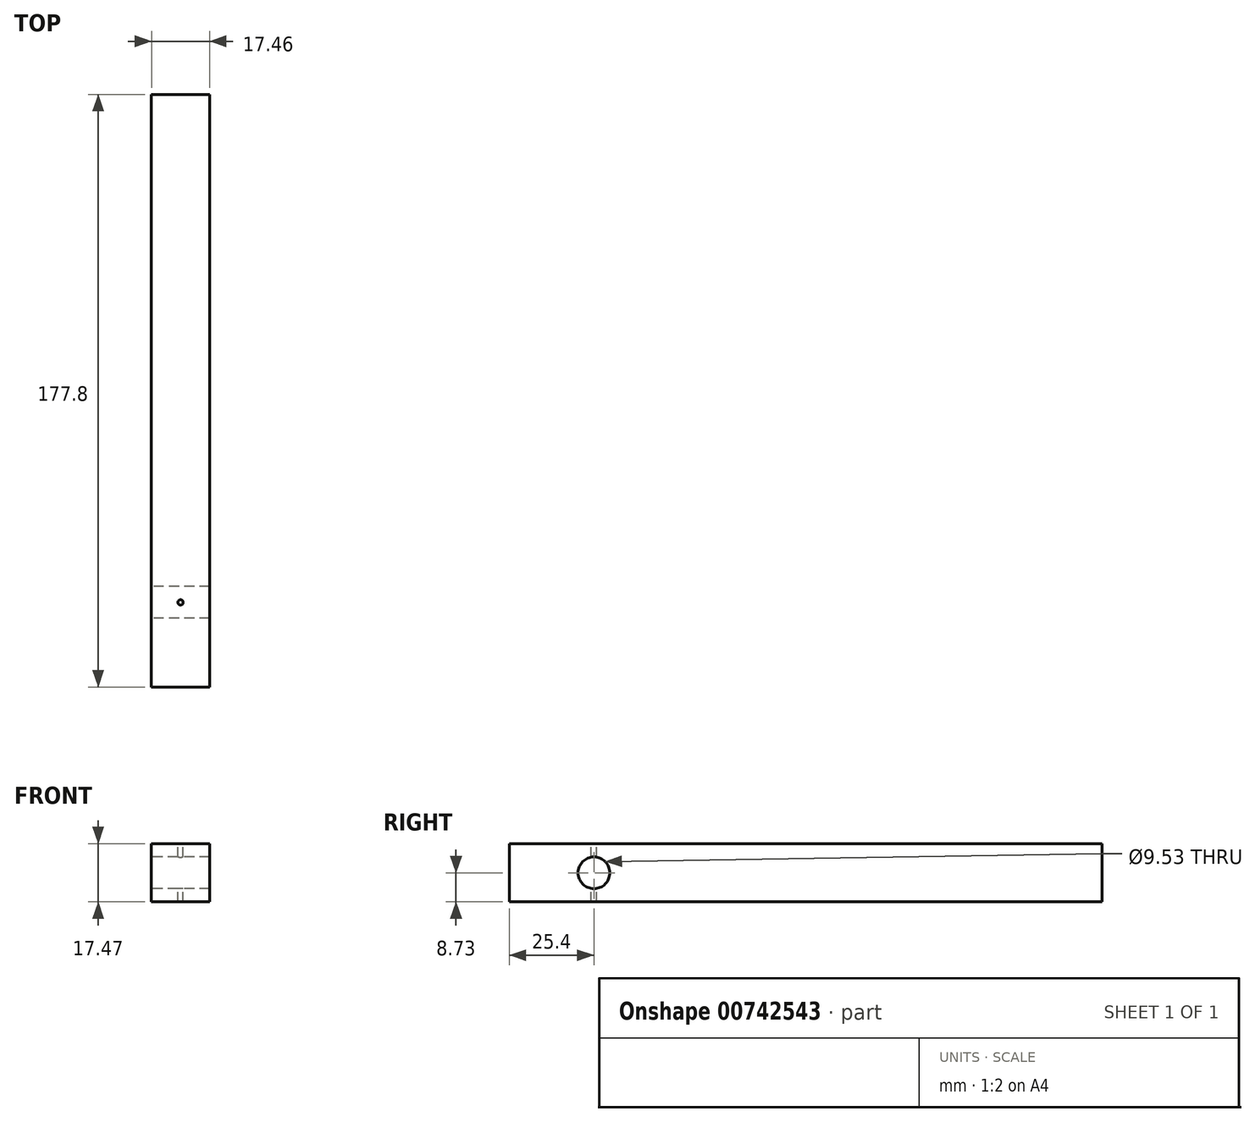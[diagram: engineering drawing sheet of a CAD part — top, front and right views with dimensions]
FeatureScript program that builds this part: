
annotation { "Feature Type Name" : "Feature", "Feature Type Description" : "" }
export const myFeature = defineFeature(function(context is Context, id is Id, definition is map)
    precondition{}
    {
        {
            var Q0;
            Q0=qCreatedBy(makeId("Front.planeOp"),FACE);
            var sketch = newSketch(context, id + "F0", { "sketchPlane" : qUnion([Q0])});
            skLineSegment(sketch, "E0", {"start": v(-17.46, 24.55) * mm, "end": v(0, 24.55) * mm});
            skLineSegment(sketch, "E1", {"start": v(-17.46, 24.55) * mm, "end": v(-17.46, 7.08) * mm});
            skLineSegment(sketch, "E2", {"start": v(-17.46, 7.08) * mm, "end": v(0, 7.08) * mm});
            skLineSegment(sketch, "E3", {"start": v(0, 7.08) * mm, "end": v(0, 24.55) * mm});
            skSolve(sketch);
        }
        {
            var Q0;
            Q0 = qSketchRegion(id + "F0", true);
            extrude(context, id + "F1", {"entities" : qUnion([Q0]), "depth" : 177.8 * mm, "offsetDistance" : 25.4 * mm});
        }
        {
            var Q0;
            Q0=makeQuery(id+"F1.opExtrude","SWEPT_FACE",FACE,{"disambiguationData":[OSD([sQuery(id+"F0.wireOp",EDGE,"E1")])]});
            var sketch = newSketch(context, id + "F2", { "sketchPlane" : qUnion([Q0])});
            skCircle(sketch, "E4", {"center": v(152.4, 15.8) * mm, "radius": 4.76 * mm});
            skSolve(sketch);
        }
        {
            var Q0;
            Q0 = qSketchRegion(id + "F2", true);
            extrude(context, id + "F3", {"entities" : qUnion([Q0]), "operationType" : NewBodyOperationType.REMOVE, "oppositeDirection" : true, "depth" : 17.48 * mm, "offsetDistance" : 25.4 * mm});
        }
        {
            var Q0;
            Q0=makeQuery(id+"F1.opExtrude","SWEPT_FACE",FACE,{"disambiguationData":[OSD([sQuery(id+"F0.wireOp",EDGE,"E0")])]});
            var sketch = newSketch(context, id + "F4", { "sketchPlane" : qUnion([Q0])});
            skCircle(sketch, "E5", {"center": v(-8.73, -152.4) * mm, "radius": 0.8 * mm});
            skSolve(sketch);
        }
        {
            var Q0;
            Q0 = qSketchRegion(id + "F4", true);
            extrude(context, id + "F5", {"entities" : qUnion([Q0]), "operationType" : NewBodyOperationType.REMOVE, "oppositeDirection" : true, "depth" : 25.4 * mm, "offsetDistance" : 25.4 * mm});
        }
    });
